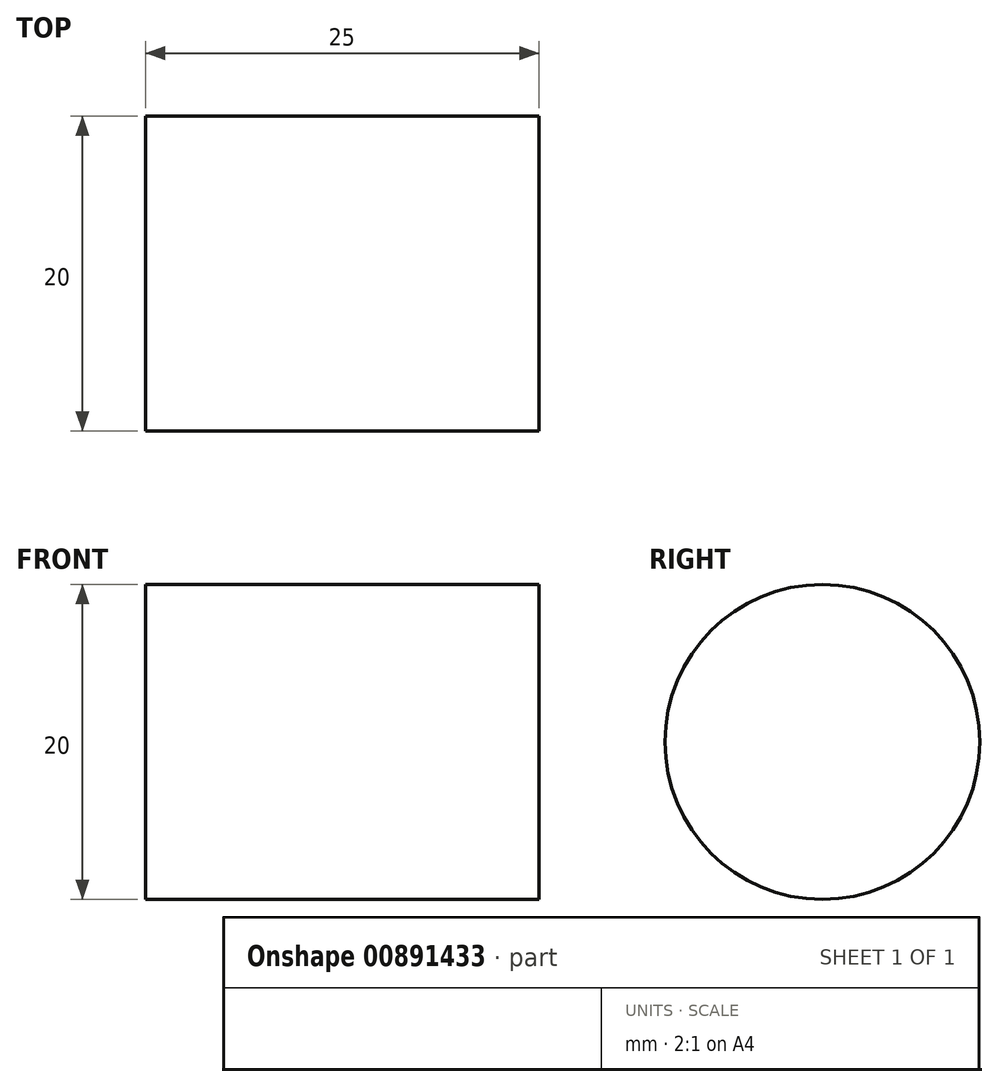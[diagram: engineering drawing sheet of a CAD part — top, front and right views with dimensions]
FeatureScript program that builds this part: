
annotation { "Feature Type Name" : "Feature", "Feature Type Description" : "" }
export const myFeature = defineFeature(function(context is Context, id is Id, definition is map)
    precondition{}
    {
        {
            var Q0;
            Q0=qCreatedBy(makeId("Right.planeOp"),FACE);
            var sketch = newSketch(context, id + "F0", { "sketchPlane" : qUnion([Q0])});
            skCircle(sketch, "E0", {"center": v(0, 0) * mm, "radius": 10 * mm});
            skSolve(sketch);
        }
        {
            var Q0;
            Q0 = qSketchRegion(id + "F0", true);
            extrude(context, id + "F1", {"entities" : qUnion([Q0]), "depth" : 25 * mm, "offsetDistance" : 25 * mm});
        }
    });
